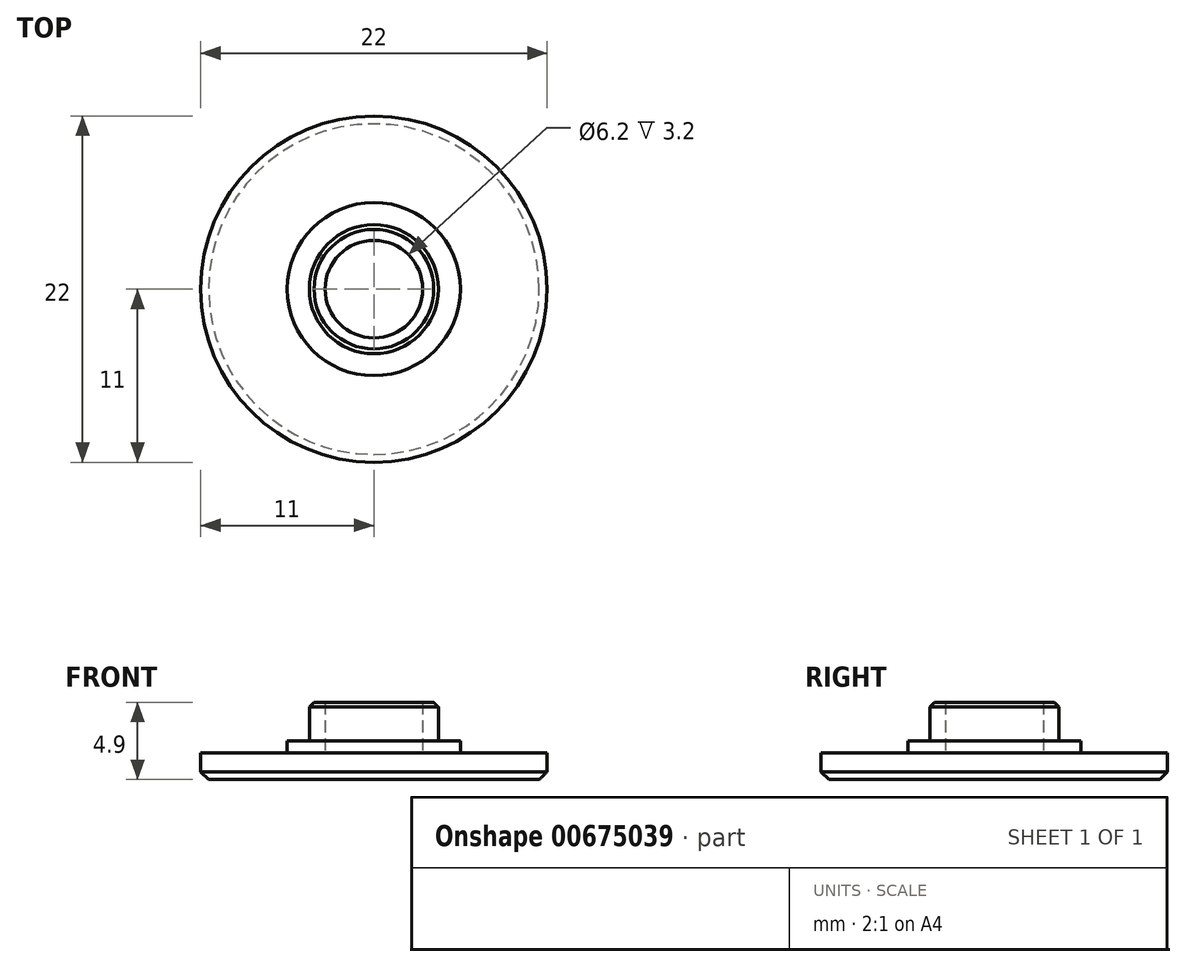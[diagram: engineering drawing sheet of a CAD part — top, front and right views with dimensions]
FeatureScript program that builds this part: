
annotation { "Feature Type Name" : "Feature", "Feature Type Description" : "" }
export const myFeature = defineFeature(function(context is Context, id is Id, definition is map)
    precondition{}
    {
        {
            var Q0;
            Q0=qCreatedBy(makeId("Top.planeOp"),FACE);
            var sketch = newSketch(context, id + "F0", { "sketchPlane" : qUnion([Q0])});
            skCircle(sketch, "E0", {"center": v(0, 0) * mm, "radius": 11 * mm});
            skCircle(sketch, "E1", {"center": v(0, 0) * mm, "radius": 4.1 * mm});
            skCircle(sketch, "E2", {"center": v(0, 0) * mm, "radius": 5.5 * mm});
            skCircle(sketch, "E3", {"center": v(0, 0) * mm, "radius": 3.1 * mm});
            skSolve(sketch);
        }
        {
            var Q0;
            Q0=makeQuery(id+"F0.imprint","IMPRINT",FACE,{"disambiguationData":[TD([[makeQuery(id+"F0.imprint","IMPRINT",EDGE,{"derivedFrom":sQuery(id+"F0.wireOp",EDGE,"E1")}),-1.0]])]});
            extrude(context, id + "F1", {"entities" : qUnion([Q0]), "depth" : 0.75 * mm, "offsetDistance" : 25 * mm});
        }
        {
            var Q0;
            Q0 = qSketchRegion(id + "F0", true);
            var Q1;
            Q1=makeQuery(id+"F0.imprint","IMPRINT",FACE,{"disambiguationData":[TD([[makeQuery(id+"F0.imprint","IMPRINT",EDGE,{"derivedFrom":sQuery(id+"F0.wireOp",EDGE,"E1")}),-1.0]])]});
            var Q2;
            Q2=makeQuery(id+"F0.imprint","IMPRINT",FACE,{"disambiguationData":[TD([[makeQuery(id+"F0.imprint","IMPRINT",EDGE,{"derivedFrom":sQuery(id+"F0.wireOp",EDGE,"E1")}),1.0]])]});
            var Q3;
            Q3=makeQuery(id+"F0.imprint","IMPRINT",FACE,{"disambiguationData":[TD([[makeQuery(id+"F0.imprint","IMPRINT",EDGE,{"derivedFrom":sQuery(id+"F0.wireOp",EDGE,"E3")}),1.0]])]});
            extrude(context, id + "F2", {"entities" : qUnion([Q0, Q1, Q2, Q3]), "operationType" : NewBodyOperationType.ADD, "oppositeDirection" : true, "depth" : 1.7 * mm, "offsetDistance" : 25 * mm});
        }
        {
            var Q0;
            Q0=makeQuery(id+"F0.imprint","IMPRINT",FACE,{"disambiguationData":[TD([[makeQuery(id+"F0.imprint","IMPRINT",EDGE,{"derivedFrom":sQuery(id+"F0.wireOp",EDGE,"E1")}),1.0]])]});
            extrude(context, id + "F3", {"entities" : qUnion([Q0]), "operationType" : NewBodyOperationType.ADD, "depth" : 3.2 * mm, "offsetDistance" : 25 * mm});
        }
        {
            var Q0;
            Q0=makeQuery(id+"F2.opExtrude","CAP_EDGE",EDGE,{"disambiguationData":[OSD([sQuery(id+"F0.wireOp",EDGE,"E0")])],"isStart":false});
            chamfer(context, id + "F4", {"entities" : qUnion([Q0]), "width" : .5 * mm, "tangentPropagation" : true});
        }
        {
            var Q0;
            Q0=makeQuery(id+"F3.opExtrude","CAP_EDGE",EDGE,{"disambiguationData":[OSD([sQuery(id+"F0.wireOp",EDGE,"E1")])],"isStart":false});
            chamfer(context, id + "F5", {"entities" : qUnion([Q0]), "width" : .3 * mm, "tangentPropagation" : true});
        }
    });
